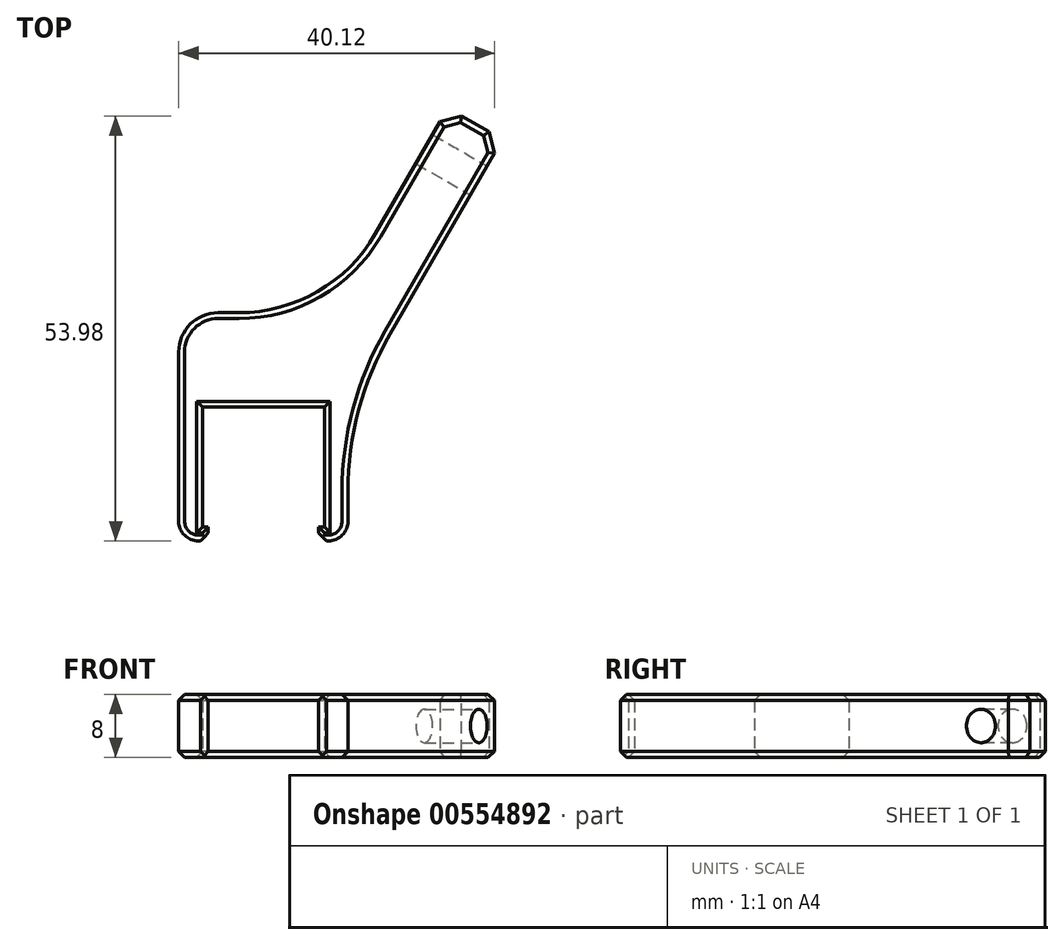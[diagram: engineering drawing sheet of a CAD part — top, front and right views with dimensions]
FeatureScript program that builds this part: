
annotation { "Feature Type Name" : "Feature", "Feature Type Description" : "" }
export const myFeature = defineFeature(function(context is Context, id is Id, definition is map)
    precondition{}
    {
        {
            var Q0;
            Q0=qCreatedBy(makeId("Top.planeOp"),FACE);
            var sketch = newSketch(context, id + "F0", { "sketchPlane" : qUnion([Q0])});
            skLineSegment(sketch, "E0", {"start": v(-7.75, -17) * mm, "end": v(-7.75, 0) * mm});
            skLineSegment(sketch, "E1", {"start": v(-7.75, 0) * mm, "end": v(7.75, 0) * mm});
            skLineSegment(sketch, "E2", {"start": v(7.75, 0) * mm, "end": v(7.75, -17) * mm});
            skLineSegment(sketch, "E3", {"start": v(7.75, -17) * mm, "end": v(10.75, -17) * mm});
            skLineSegment(sketch, "E4", {"start": v(10.75, -17) * mm, "end": v(10.75, 0) * mm});
            skLineSegment(sketch, "E5", {"start": v(10.75, 0) * mm, "end": v(30.37, 33.98) * mm});
            skLineSegment(sketch, "E6", {"start": v(30.37, 33.98) * mm, "end": v(23.44, 37.98) * mm});
            skLineSegment(sketch, "E7", {"start": v(23.44, 37.98) * mm, "end": v(8.44, 12) * mm});
            skLineSegment(sketch, "E8", {"start": v(8.44, 12) * mm, "end": v(-10.75, 12) * mm});
            skLineSegment(sketch, "E9", {"start": v(-10.75, 12) * mm, "end": v(-10.75, -17) * mm});
            skLineSegment(sketch, "E10", {"start": v(-10.75, -17) * mm, "end": v(-7.75, -17) * mm});
            skLineSegment(sketch, "E11", {"start": v(0, 0) * mm, "end": v(0, -29.95) * mm, "construction": true});
            skLineSegment(sketch, "E12", {"start": v(-7.75, -15.25) * mm, "end": v(-7, -15.25) * mm});
            skLineSegment(sketch, "E13", {"start": v(-7, -15.25) * mm, "end": v(-7, -17) * mm});
            skLineSegment(sketch, "E14", {"start": v(-7, -17) * mm, "end": v(-7.75, -17) * mm});
            skLineSegment(sketch, "E15", {"start": v(7.75, -17) * mm, "end": v(7, -17) * mm});
            skLineSegment(sketch, "E16", {"start": v(7, -17) * mm, "end": v(7, -15.25) * mm});
            skLineSegment(sketch, "E17", {"start": v(7, -15.25) * mm, "end": v(7.75, -15.25) * mm});
            skSolve(sketch);
        }
        {
            var Q0;
            Q0=makeQuery(id+"F0.imprint","IMPRINT",FACE,{"disambiguationData":[TD([[makeQuery(id+"F0.imprint","IMPRINT",EDGE,{"derivedFrom":sQuery(id+"F0.wireOp",EDGE,"E0")}),1.0]])]});
            var Q1;
            {var subQ2=sQuery(id+"F0.wireOp",EDGE,"E12");Q1=makeQuery(id+"F0.imprint","IMPRINT",FACE,{"disambiguationData":[TD([[makeQuery(id+"F0.imprint","IMPRINT",EDGE,{"derivedFrom":subQ2}),-1.0]])]});}
            var Q2;
            {var subQ0=sQuery(id+"F0.wireOp",EDGE,"E15");Q2=makeQuery(id+"F0.imprint","IMPRINT",FACE,{"disambiguationData":[TD([[makeQuery(id+"F0.imprint","IMPRINT",EDGE,{"derivedFrom":subQ0}),-1.0]])]});}
            extrude(context, id + "F1", {"entities" : qUnion([Q0, Q1, Q2]), "depth" : 8 * mm, "offsetDistance" : 25 * mm});
        }
        {
            var Q0;
            Q0=makeQuery(id+"F1.opExtrude","SWEPT_EDGE",EDGE,{"disambiguationData":[OSD([sQuery(id+"F0.wireOp",EDGE,"E4"),sQuery(id+"F0.wireOp",EDGE,"E5")])]});
            fillet(context, id + "F2", {"entities" : qUnion([Q0]), "radius" : 40 * mm, "tangentPropagation" : true, "allowEdgeOverflow" : false});
        }
        {
            var Q0;
            Q0=makeQuery(id+"F1.opExtrude","SWEPT_EDGE",EDGE,{"disambiguationData":[OSD([sQuery(id+"F0.wireOp",EDGE,"E7"),sQuery(id+"F0.wireOp",EDGE,"E8")])]});
            fillet(context, id + "F3", {"entities" : qUnion([Q0]), "radius" : 20 * mm, "tangentPropagation" : true, "allowEdgeOverflow" : false});
        }
        {
            var Q0;
            Q0=makeQuery(id+"F1.opExtrude","SWEPT_EDGE",EDGE,{"disambiguationData":[OSD([sQuery(id+"F0.wireOp",EDGE,"E8"),sQuery(id+"F0.wireOp",EDGE,"E9")])]});
            fillet(context, id + "F4", {"entities" : qUnion([Q0]), "radius" : 5 * mm, "tangentPropagation" : true, "allowEdgeOverflow" : false});
        }
        {
            var Q0;
            Q0=makeQuery(id+"F1.opExtrude","SWEPT_EDGE",EDGE,{"disambiguationData":[OSD([sQuery(id+"F0.wireOp",EDGE,"E3"),sQuery(id+"F0.wireOp",EDGE,"E4")])]});
            var Q1;
            Q1=makeQuery(id+"F1.opExtrude","SWEPT_EDGE",EDGE,{"disambiguationData":[OSD([sQuery(id+"F0.wireOp",EDGE,"E9"),sQuery(id+"F0.wireOp",EDGE,"E10")])]});
            fillet(context, id + "F5", {"entities" : qUnion([Q0, Q1]), "radius" : 2.5 * mm, "tangentPropagation" : true, "allowEdgeOverflow" : false});
        }
        {
            var Q0;
            Q0=makeQuery(id+"F1.opExtrude","SWEPT_EDGE",EDGE,{"disambiguationData":[OSD([sQuery(id+"F0.wireOp",EDGE,"E5"),sQuery(id+"F0.wireOp",EDGE,"E6")])]});
            var Q1;
            Q1=makeQuery(id+"F1.opExtrude","SWEPT_EDGE",EDGE,{"disambiguationData":[OSD([sQuery(id+"F0.wireOp",EDGE,"E6"),sQuery(id+"F0.wireOp",EDGE,"E7")])]});
            chamfer(context, id + "F6", {"entities" : qUnion([Q0, Q1]), "width" : 2 * mm, "tangentPropagation" : true});
        }
        {
            var Q0;
            Q0=makeQuery(id+"F1.opExtrude","SWEPT_FACE",FACE,{"disambiguationData":[OSD([sQuery(id+"F0.wireOp",EDGE,"E5")])]});
            var sketch = newSketch(context, id + "F7", { "sketchPlane" : qUnion([Q0])});
            skCircle(sketch, "E18", {"center": v(38.61, 4) * mm, "radius": 2.12 * mm});
            skLineSegment(sketch, "E19", {"start": v(38.61, 4) * mm, "end": v(42.61, 4) * mm});
            skSolve(sketch);
        }
        {
            var Q0;
            Q0=makeQuery(id+"F7.imprint","IMPRINT",FACE,{"disambiguationData":[TD([[makeQuery(id+"F7.imprint","IMPRINT",EDGE,{"derivedFrom":sQuery(id+"F7.wireOp",EDGE,"E18")}),1.0]])]});
            extrude(context, id + "F8", {"entities" : qUnion([Q0]), "operationType" : NewBodyOperationType.REMOVE, "endBound" : BoundingType.THROUGH_ALL, "oppositeDirection" : true, "depth" : 25 * mm, "offsetDistance" : 25 * mm});
        }
        {
            var Q0;
            Q0=makeQuery(id+"F1.opExtrude","CAP_FACE",FACE,{"disambiguationData":[OSD([sQuery(id+"F0.wireOp",EDGE,"E0"),sQuery(id+"F0.wireOp",EDGE,"E1"),sQuery(id+"F0.wireOp",EDGE,"E2"),sQuery(id+"F0.wireOp",EDGE,"E3"),sQuery(id+"F0.wireOp",EDGE,"E4"),sQuery(id+"F0.wireOp",EDGE,"E5"),sQuery(id+"F0.wireOp",EDGE,"E6"),sQuery(id+"F0.wireOp",EDGE,"E7"),sQuery(id+"F0.wireOp",EDGE,"E8"),sQuery(id+"F0.wireOp",EDGE,"E9"),sQuery(id+"F0.wireOp",EDGE,"E10"),sQuery(id+"F0.wireOp",EDGE,"E12"),sQuery(id+"F0.wireOp",EDGE,"E13"),sQuery(id+"F0.wireOp",EDGE,"E14"),sQuery(id+"F0.wireOp",EDGE,"E15"),sQuery(id+"F0.wireOp",EDGE,"E16"),sQuery(id+"F0.wireOp",EDGE,"E17")])],"isStart":false});
            var Q1;
            Q1=makeQuery(id+"F1.opExtrude","CAP_FACE",FACE,{"disambiguationData":[OSD([sQuery(id+"F0.wireOp",EDGE,"E0"),sQuery(id+"F0.wireOp",EDGE,"E1"),sQuery(id+"F0.wireOp",EDGE,"E2"),sQuery(id+"F0.wireOp",EDGE,"E3"),sQuery(id+"F0.wireOp",EDGE,"E4"),sQuery(id+"F0.wireOp",EDGE,"E5"),sQuery(id+"F0.wireOp",EDGE,"E6"),sQuery(id+"F0.wireOp",EDGE,"E7"),sQuery(id+"F0.wireOp",EDGE,"E8"),sQuery(id+"F0.wireOp",EDGE,"E9"),sQuery(id+"F0.wireOp",EDGE,"E10"),sQuery(id+"F0.wireOp",EDGE,"E12"),sQuery(id+"F0.wireOp",EDGE,"E13"),sQuery(id+"F0.wireOp",EDGE,"E14"),sQuery(id+"F0.wireOp",EDGE,"E15"),sQuery(id+"F0.wireOp",EDGE,"E16"),sQuery(id+"F0.wireOp",EDGE,"E17")])],"isStart":true});
            chamfer(context, id + "F9", {"entities" : qUnion([Q0, Q1]), "width" : 0.75 * mm, "tangentPropagation" : true});
        }
        {
            var Q0;
            Q0=makeQuery(id+"F1.opExtrude","SWEPT_EDGE",EDGE,{"disambiguationData":[OSD([sQuery(id+"F0.wireOp",EDGE,"E13"),sQuery(id+"F0.wireOp",EDGE,"E14")])]});
            var Q1;
            Q1=makeQuery(id+"F1.opExtrude","SWEPT_EDGE",EDGE,{"disambiguationData":[OSD([sQuery(id+"F0.wireOp",EDGE,"E15"),sQuery(id+"F0.wireOp",EDGE,"E16")])]});
            chamfer(context, id + "F10", {"entities" : qUnion([Q0, Q1]), "width" : 1 * mm, "tangentPropagation" : true});
        }
    });
